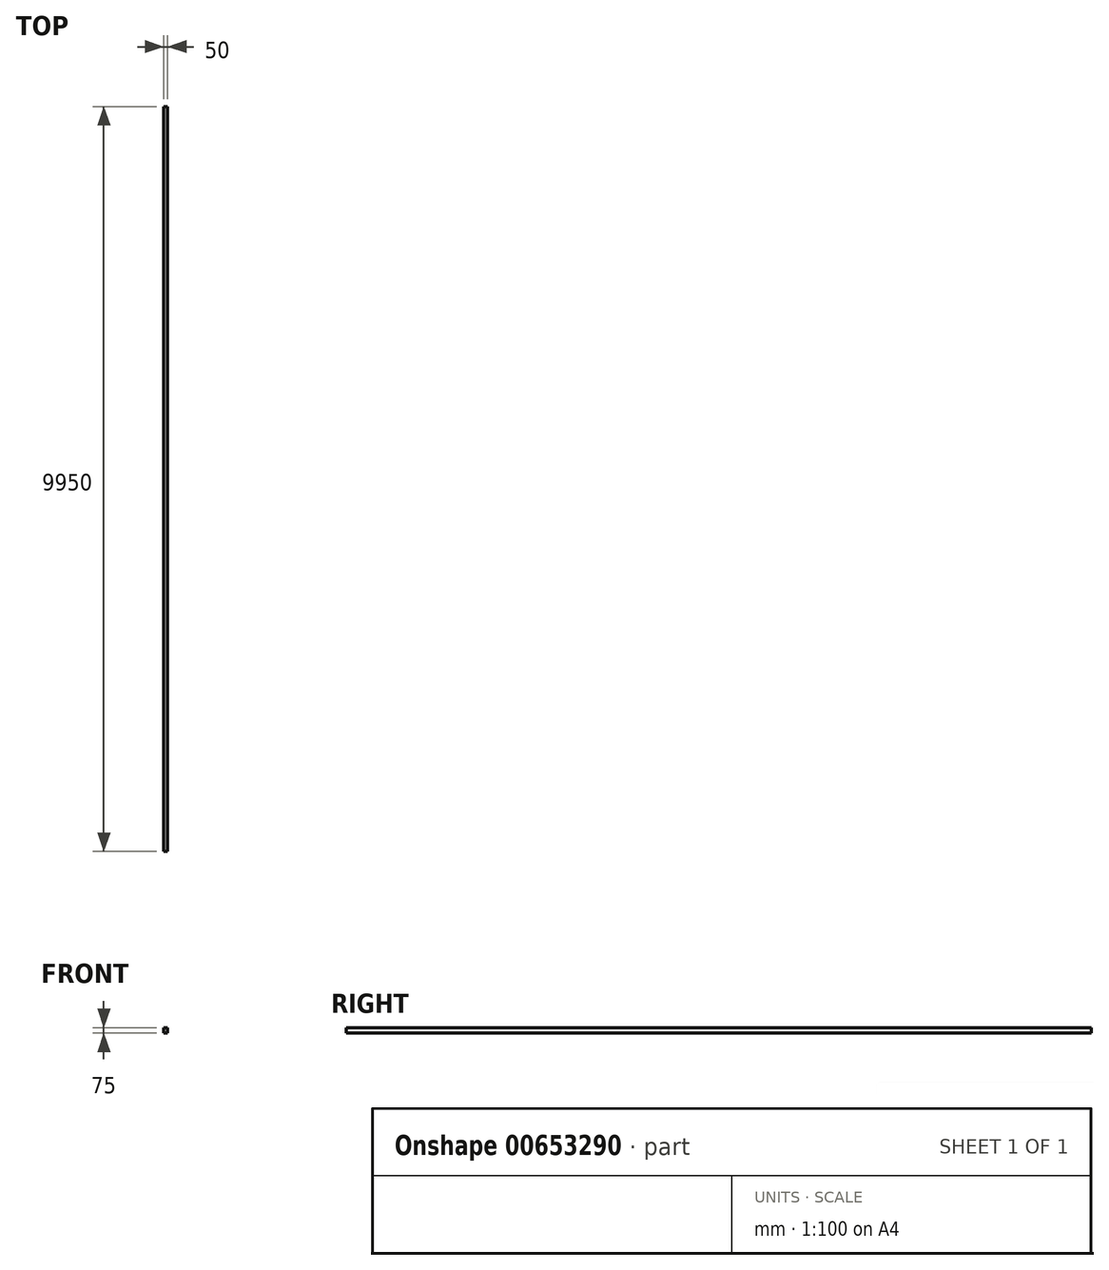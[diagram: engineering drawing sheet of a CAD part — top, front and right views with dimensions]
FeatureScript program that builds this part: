
annotation { "Feature Type Name" : "Feature", "Feature Type Description" : "" }
export const myFeature = defineFeature(function(context is Context, id is Id, definition is map)
    precondition{}
    {
        {
            var Q0;
            Q0=qCreatedBy(makeId("Front.planeOp"),FACE);
            var sketch = newSketch(context, id + "F0", { "sketchPlane" : qUnion([Q0])});
            skLineSegment(sketch, "E0.bottom", {"start": v(0, 0) * mm, "end": v(50, 0) * mm});
            skLineSegment(sketch, "E0.top", {"start": v(0, 75) * mm, "end": v(50, 75) * mm});
            skLineSegment(sketch, "E0.left", {"start": v(0, 0) * mm, "end": v(0, 75) * mm});
            skLineSegment(sketch, "E0.right", {"start": v(50, 0) * mm, "end": v(50, 75) * mm});
            skSolve(sketch);
        }
        {
            var Q0;
            Q0=makeQuery(id+"F0.imprint","IMPRINT",FACE,{"disambiguationData":[TD([[makeQuery(id+"F0.imprint","IMPRINT",EDGE,{"derivedFrom":sQuery(id+"F0.wireOp",EDGE,"E0.bottom")}),1.0]])]});
            extrude(context, id + "F1", {"entities" : qUnion([Q0]), "depth" : 9950 * mm, "offsetDistance" : 25 * mm, "symmetric" : true});
        }
    });
